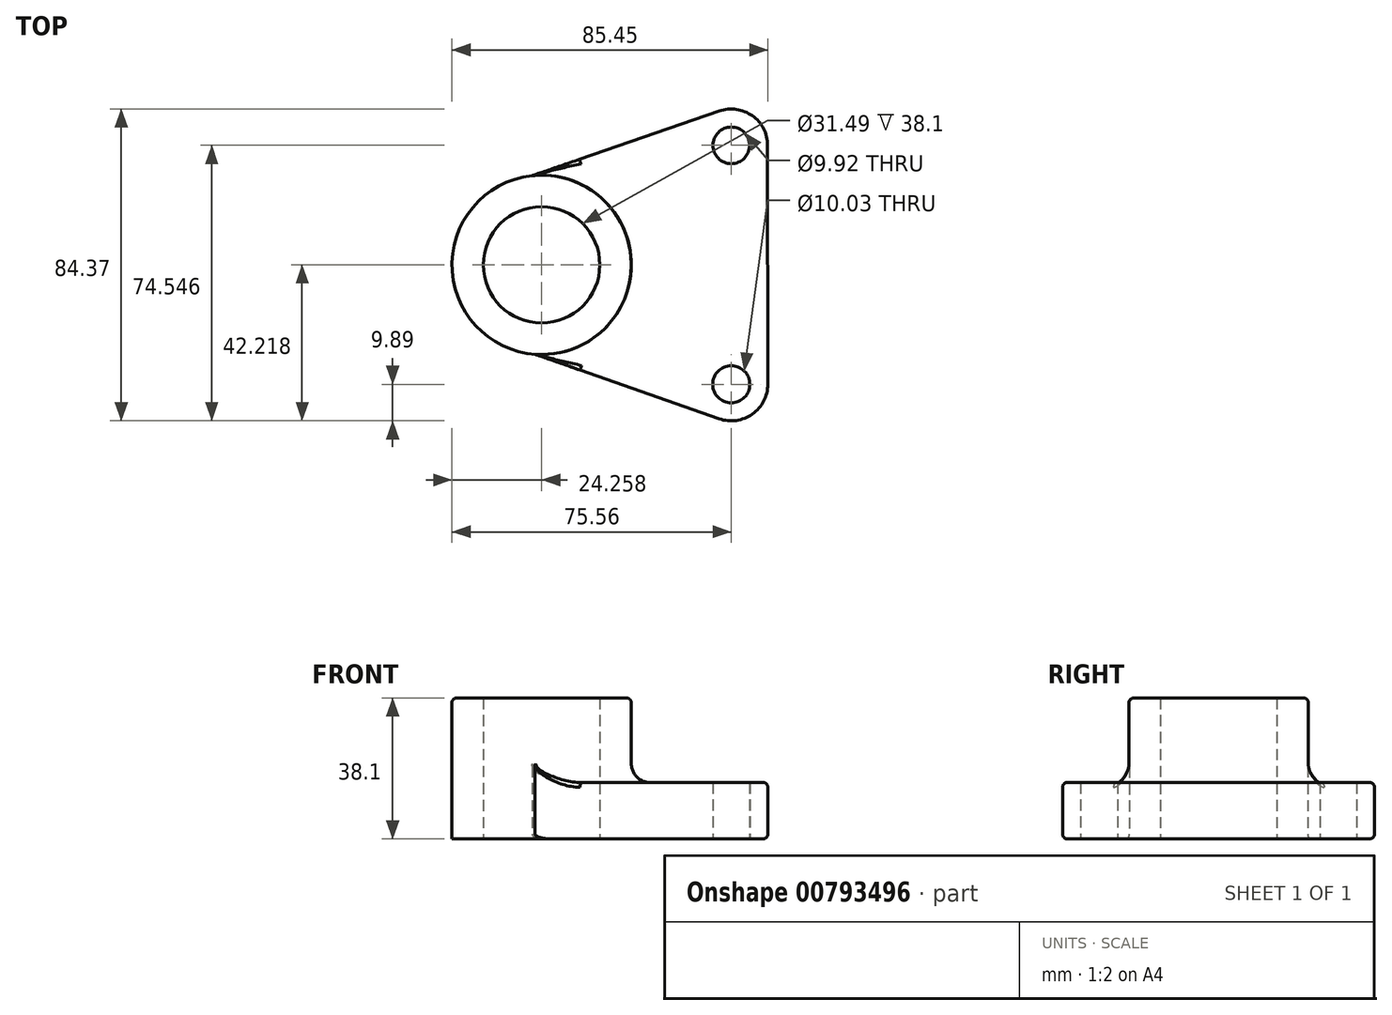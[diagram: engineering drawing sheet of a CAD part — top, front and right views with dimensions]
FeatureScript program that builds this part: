
annotation { "Feature Type Name" : "Feature", "Feature Type Description" : "" }
export const myFeature = defineFeature(function(context is Context, id is Id, definition is map)
    precondition{}
    {
        {
            var Q0;
            Q0=qCreatedBy(makeId("Top.planeOp"),FACE);
            var sketch = newSketch(context, id + "F0", { "sketchPlane" : qUnion([Q0])});
            skLineSegment(sketch, "E0", {"start": v(0, 0) * mm, "end": v(0, 64.66) * mm});
            skCircle(sketch, "E1", {"center": v(0, 0) * mm, "radius": 9.89 * mm});
            skCircle(sketch, "E2", {"center": v(0, 64.66) * mm, "radius": 9.82 * mm});
            skLineSegment(sketch, "E3", {"start": v(0, 32.33) * mm, "end": v(-51.3, 32.33) * mm});
            skCircle(sketch, "E4", {"center": v(-51.3, 32.33) * mm, "radius": 24.26 * mm});
            skLineSegment(sketch, "E5", {"start": v(-53.9, 56.45) * mm, "end": v(0, 75.04) * mm});
            skLineSegment(sketch, "E6", {"start": v(-53.1, 8.14) * mm, "end": v(0, -10.47) * mm});
            skLineSegment(sketch, "E7", {"start": v(9.89, 0) * mm, "end": v(9.82, 64.67) * mm});
            skCircle(sketch, "E8", {"center": v(-51.3, 32.33) * mm, "radius": 15.74 * mm});
            skCircle(sketch, "E9", {"center": v(0, 64.66) * mm, "radius": 4.96 * mm});
            skCircle(sketch, "E10", {"center": v(0, 0) * mm, "radius": 5.02 * mm});
            skSolve(sketch);
        }
        {
            var Q0;
            Q0=makeQuery(id+"F0.imprint","IMPRINT",FACE,{"disambiguationData":[TD([[makeQuery(id+"F0.imprint","IMPRINT",EDGE,{"derivedFrom":sQuery(id+"F0.wireOp",EDGE,"E8")}),-1.0]])]});
            extrude(context, id + "F1", {"entities" : qUnion([Q0]), "depth" : 38.1 * mm, "offsetDistance" : 25.4 * mm});
        }
        {
            var Q0;
            Q0 = qSketchRegion(id + "F0", true);
            extrude(context, id + "F2", {"entities" : qUnion([Q0]), "operationType" : NewBodyOperationType.ADD, "depth" : 15.24 * mm, "offsetDistance" : 25.4 * mm});
        }
        {
            var Q0;
            Q0=makeQuery(id+"F1.opExtrude","CAP_EDGE",EDGE,{"disambiguationData":[OSD([sQuery(id+"F0.wireOp",EDGE,"E4")])],"isStart":false});
            fillet(context, id + "F3", {"entities" : qUnion([Q0]), "radius" : 1.27 * mm, "tangentPropagation" : true, "allowEdgeOverflow" : false});
        }
        {
            var Q0;
            {var subQ0=sQuery(id+"F0.wireOp",EDGE,"E4");Q0=makeQuery(id+"F2.boolean.opBoolean","INTERSECT",EDGE,{"derivedFrom":[makeQuery(id+"F1.opExtrude","SWEPT_FACE",FACE,{"disambiguationData":[OSD([subQ0])]}),makeQuery(id+"F2.opExtrude","CAP_FACE",FACE,{"disambiguationData":[OSD([sQuery(id+"F0.wireOp",EDGE,"E1"),sQuery(id+"F0.wireOp",EDGE,"E2"),subQ0,sQuery(id+"F0.wireOp",EDGE,"E5"),sQuery(id+"F0.wireOp",EDGE,"E6"),sQuery(id+"F0.wireOp",EDGE,"E7"),sQuery(id+"F0.wireOp",EDGE,"E8"),sQuery(id+"F0.wireOp",EDGE,"E9"),sQuery(id+"F0.wireOp",EDGE,"E10")])],"isStart":false})]});}
            var Q1;
            Q1=makeQuery(id+"F2.opExtrude","SWEPT_EDGE",EDGE,{"disambiguationData":[OSD([sQuery(id+"F0.wireOp",EDGE,"E4"),sQuery(id+"F0.wireOp",EDGE,"E6")])]});
            var Q2;
            Q2=makeQuery(id+"F2.opExtrude","SWEPT_EDGE",EDGE,{"disambiguationData":[OSD([sQuery(id+"F0.wireOp",EDGE,"E4"),sQuery(id+"F0.wireOp",EDGE,"E5")])]});
            fillet(context, id + "F4", {"entities" : qUnion([Q0, Q1, Q2]), "radius" : 5.08 * mm, "tangentPropagation" : true, "allowEdgeOverflow" : false});
        }
        {
            var Q0;
            Q0=makeQuery(id+"F2.opExtrude","CAP_EDGE",EDGE,{"disambiguationData":[OSD([sQuery(id+"F0.wireOp",EDGE,"E5")])],"isStart":false});
            var Q1;
            Q1=makeQuery(id+"F2.opExtrude","CAP_EDGE",EDGE,{"disambiguationData":[OSD([sQuery(id+"F0.wireOp",EDGE,"E5")])],"isStart":true});
            fillet(context, id + "F5", {"entities" : qUnion([Q0, Q1]), "radius" : 1.27 * mm, "tangentPropagation" : true, "allowEdgeOverflow" : false});
        }
    });
